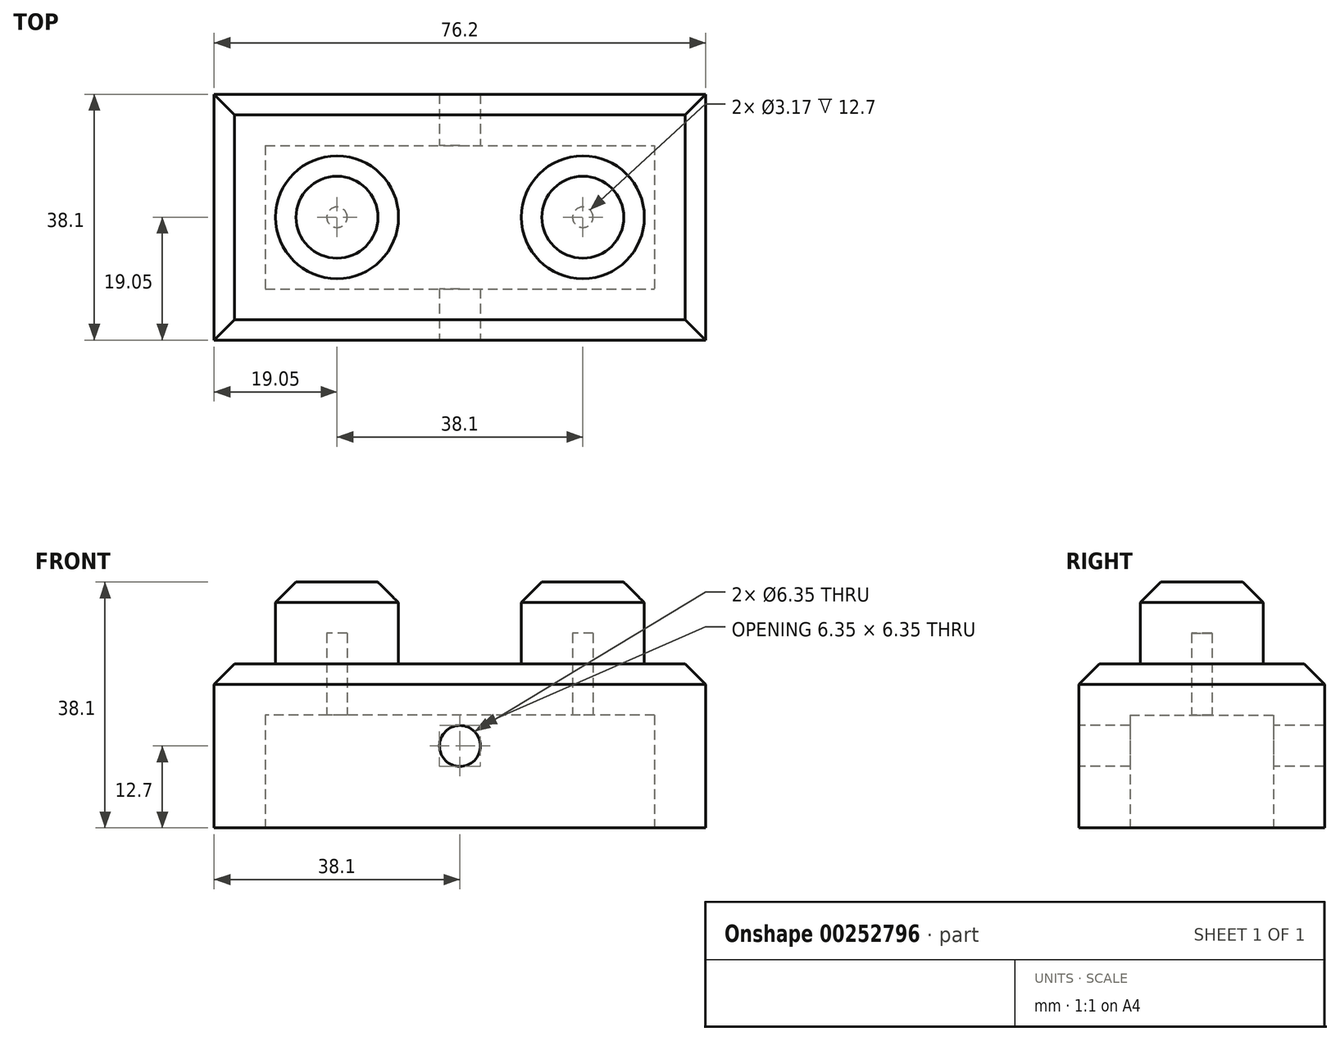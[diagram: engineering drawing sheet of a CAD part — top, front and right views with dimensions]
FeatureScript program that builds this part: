
annotation { "Feature Type Name" : "Feature", "Feature Type Description" : "" }
export const myFeature = defineFeature(function(context is Context, id is Id, definition is map)
    precondition{}
    {
        {
            var Q0;
            Q0=qCreatedBy(makeId("Top.planeOp"),FACE);
            var sketch = newSketch(context, id + "F0", { "sketchPlane" : qUnion([Q0])});
            skLineSegment(sketch, "E0.bottom", {"start": v(0, 0) * mm, "end": v(76.2, 0) * mm});
            skLineSegment(sketch, "E0.top", {"start": v(0, -38.1) * mm, "end": v(76.2, -38.1) * mm});
            skLineSegment(sketch, "E0.left", {"start": v(0, 0) * mm, "end": v(0, -38.1) * mm});
            skLineSegment(sketch, "E0.right", {"start": v(76.2, 0) * mm, "end": v(76.2, -38.1) * mm});
            skSolve(sketch);
        }
        {
            var Q0;
            Q0=makeQuery(id+"F0.imprint","IMPRINT",FACE,{"disambiguationData":[TD([[makeQuery(id+"F0.imprint","IMPRINT",EDGE,{"derivedFrom":sQuery(id+"F0.wireOp",EDGE,"E0.bottom")}),-1.0]])]});
            extrude(context, id + "F1", {"entities" : qUnion([Q0]), "depth" : 25.4 * mm});
        }
        {
            var Q0;
            Q0=makeQuery(id+"F1.opExtrude","CAP_FACE",FACE,{"disambiguationData":[OSD([sQuery(id+"F0.wireOp",EDGE,"E0.bottom"),sQuery(id+"F0.wireOp",EDGE,"E0.top"),sQuery(id+"F0.wireOp",EDGE,"E0.left"),sQuery(id+"F0.wireOp",EDGE,"E0.right")])],"isStart":false});
            var sketch = newSketch(context, id + "F2", { "sketchPlane" : qUnion([Q0])});
            skCircle(sketch, "E1", {"center": v(57.15, -19.05) * mm, "radius": 9.53 * mm});
            skCircle(sketch, "E2", {"center": v(19.05, -19.05) * mm, "radius": 9.53 * mm});
            skSolve(sketch);
        }
        {
            var Q0;
            Q0 = qSketchRegion(id + "F2", true);
            extrude(context, id + "F3", {"entities" : qUnion([Q0]), "operationType" : NewBodyOperationType.ADD, "depth" : 12.7 * mm});
        }
        {
            var Q0;
            Q0=makeQuery(id+"F3.opExtrude","CAP_EDGE",EDGE,{"disambiguationData":[OSD([sQuery(id+"F2.wireOp",EDGE,"E2")])],"isStart":false});
            var Q1;
            Q1=makeQuery(id+"F3.opExtrude","CAP_EDGE",EDGE,{"disambiguationData":[OSD([sQuery(id+"F2.wireOp",EDGE,"E1")])],"isStart":false});
            var Q2;
            Q2=makeQuery(id+"F1.opExtrude","CAP_EDGE",EDGE,{"disambiguationData":[OSD([sQuery(id+"F0.wireOp",EDGE,"E0.right")])],"isStart":false});
            var Q3;
            Q3=makeQuery(id+"F1.opExtrude","CAP_EDGE",EDGE,{"disambiguationData":[OSD([sQuery(id+"F0.wireOp",EDGE,"E0.top")])],"isStart":false});
            var Q4;
            Q4=makeQuery(id+"F1.opExtrude","CAP_EDGE",EDGE,{"disambiguationData":[OSD([sQuery(id+"F0.wireOp",EDGE,"E0.left")])],"isStart":false});
            var Q5;
            Q5=makeQuery(id+"F1.opExtrude","CAP_EDGE",EDGE,{"disambiguationData":[OSD([sQuery(id+"F0.wireOp",EDGE,"E0.bottom")])],"isStart":false});
            chamfer(context, id + "F4", {"entities" : qUnion([Q0, Q1, Q2, Q3, Q4, Q5]), "chamferType" : ChamferType.OFFSET_ANGLE, "width" : 3.17 * mm, "oppositeDirection" : false, "angle" : 45 * degree, "tangentPropagation" : true});
        }
        {
            var Q0;
            Q0=makeQuery(id+"F1.opExtrude","CAP_FACE",FACE,{"disambiguationData":[OSD([sQuery(id+"F0.wireOp",EDGE,"E0.bottom"),sQuery(id+"F0.wireOp",EDGE,"E0.top"),sQuery(id+"F0.wireOp",EDGE,"E0.left"),sQuery(id+"F0.wireOp",EDGE,"E0.right")])],"isStart":true});
            shell(context, id + "F5", {"entities" : qUnion([Q0]), "thickness" : 7.94 * mm});
        }
        {
            var Q0;
            Q0=makeQuery(id+"F1.opExtrude","SWEPT_FACE",FACE,{"disambiguationData":[OSD([sQuery(id+"F0.wireOp",EDGE,"E0.top")])]});
            var sketch = newSketch(context, id + "F6", { "sketchPlane" : qUnion([Q0])});
            skCircle(sketch, "E3", {"center": v(38.1, 12.7) * mm, "radius": 3.18 * mm});
            skSolve(sketch);
        }
        {
            var Q0;
            Q0 = qSketchRegion(id + "F6", true);
            extrude(context, id + "F7", {"entities" : qUnion([Q0]), "operationType" : NewBodyOperationType.REMOVE, "oppositeDirection" : true, "depth" : 38.1 * mm});
        }
    });
